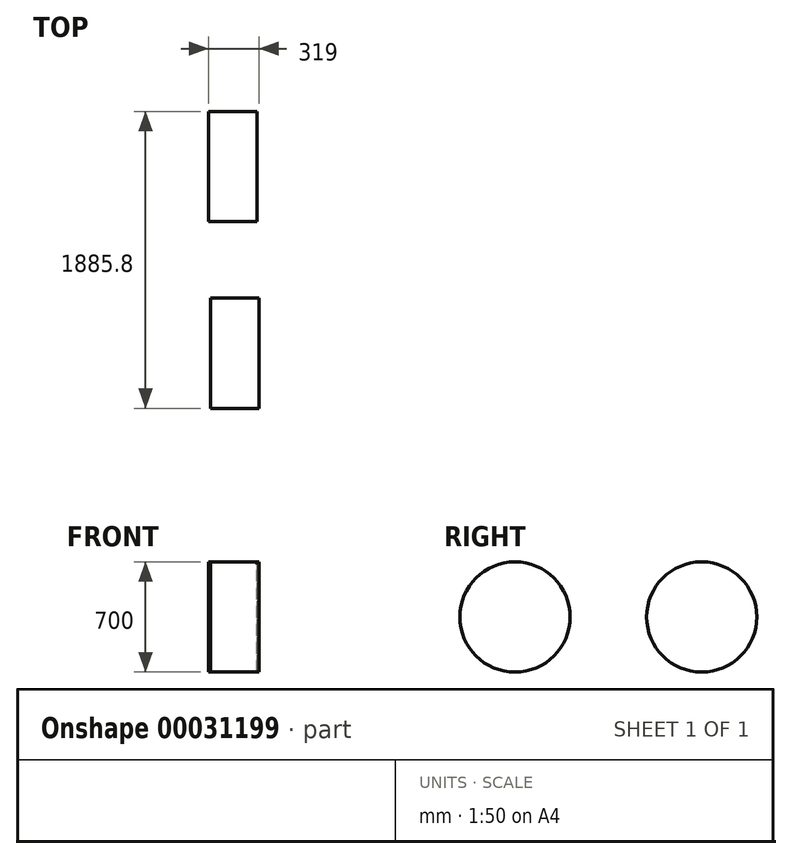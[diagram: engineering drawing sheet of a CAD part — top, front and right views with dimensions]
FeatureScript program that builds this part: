
annotation { "Feature Type Name" : "Feature", "Feature Type Description" : "" }
export const myFeature = defineFeature(function(context is Context, id is Id, definition is map)
    precondition{}
    {
        {
            var Q0;
            Q0=qCreatedBy(makeId("Right.planeOp"),FACE);
            var sketch = newSketch(context, id + "F0", { "sketchPlane" : qUnion([Q0])});
            skCircle(sketch, "E0", {"center": v(0, 0) * mm, "radius": 350 * mm});
            skCircle(sketch, "E1", {"center": v(-1185.8, 0) * mm, "radius": 350 * mm});
            skLineSegment(sketch, "E2", {"start": v(0, 0) * mm, "end": v(-385.91, 522.72) * mm});
            skLineSegment(sketch, "E3", {"start": v(-385.91, 522.72) * mm, "end": v(-438.2, -75) * mm});
            skLineSegment(sketch, "E4", {"start": v(-438.2, -75) * mm, "end": v(0, 0) * mm});
            skLineSegment(sketch, "E5", {"start": v(-1185.8, 0) * mm, "end": v(-1035.91, 522.72) * mm});
            skLineSegment(sketch, "E6", {"start": v(-1035.91, 522.72) * mm, "end": v(-385.91, 522.72) * mm});
            skLineSegment(sketch, "E7", {"start": v(-438.2, -75) * mm, "end": v(-1067.6, 412.17) * mm});
            skLineSegment(sketch, "E8", {"start": v(0, -350) * mm, "end": v(-1656.6, -350) * mm, "construction": true});
            skLineSegment(sketch, "E9", {"start": v(-385.91, 522.72) * mm, "end": v(-370.22, 702.03) * mm});
            skLineSegment(sketch, "E10", {"start": v(-305.2, 702.03) * mm, "end": v(-504.04, 702.03) * mm});
            skCircle(sketch, "E11", {"center": v(-438.2, -75) * mm, "radius": 170 * mm, "construction": true});
            skSolve(sketch);
        }
        {
            var Q0;
            Q0=makeQuery(id+"F0.imprint","IMPRINT",FACE,{"disambiguationData":[TD([[makeQuery(id+"F0.imprint","IMPRINT",EDGE,{"derivedFrom":sQuery(id+"F0.wireOp",EDGE,"E1")}),1.0]])]});
            extrude(context, id + "F1", {"entities" : qUnion([Q0]), "endBound" : BoundingType.SYMMETRIC, "depth" : 25 * mm});
        }
        {
            var Q0;
            Q0=makeQuery(id+"F1.opExtrude","CAP_FACE",FACE,{"disambiguationData":[OSD([sQuery(id+"F0.wireOp",EDGE,"E1")])],"isStart":false});
            var Q1;
            {var subQ1=sQuery(id+"F0.wireOp",EDGE,"E0");var subQ3=sQuery(id+"F0.wireOp",EDGE,"E2");var subQ5=makeQuery(id+"F0.imprint","INTERSECT",VERTEX,{"derivedFrom":[subQ1,subQ3]});Q1=makeQuery(id+"F0.imprint","IMPRINT",FACE,{"disambiguationData":[TD([[makeQuery(id+"F0.imprint","IMPRINT",EDGE,{"disambiguationData":[TD([[subQ5,1.0]])],"derivedFrom":subQ1}),1.0]])]});}
            var Q2;
            {var subQ0=sQuery(id+"F0.wireOp",EDGE,"E2");var subQ1=sQuery(id+"F0.wireOp",EDGE,"E0");var subQ2=makeQuery(id+"F0.imprint","INTERSECT",VERTEX,{"derivedFrom":[subQ1,subQ0]});Q2=makeQuery(id+"F0.imprint","IMPRINT",FACE,{"disambiguationData":[TD([[makeQuery(id+"F0.imprint","IMPRINT",EDGE,{"disambiguationData":[TD([[subQ2,-1.0]])],"derivedFrom":subQ1}),1.0]])]});}
            extrude(context, id + "F2", {"entities" : qUnion([Q0, Q1, Q2]), "operationType" : NewBodyOperationType.ADD, "endBound" : BoundingType.SYMMETRIC, "depth" : 306.5 * mm});
        }
    });
